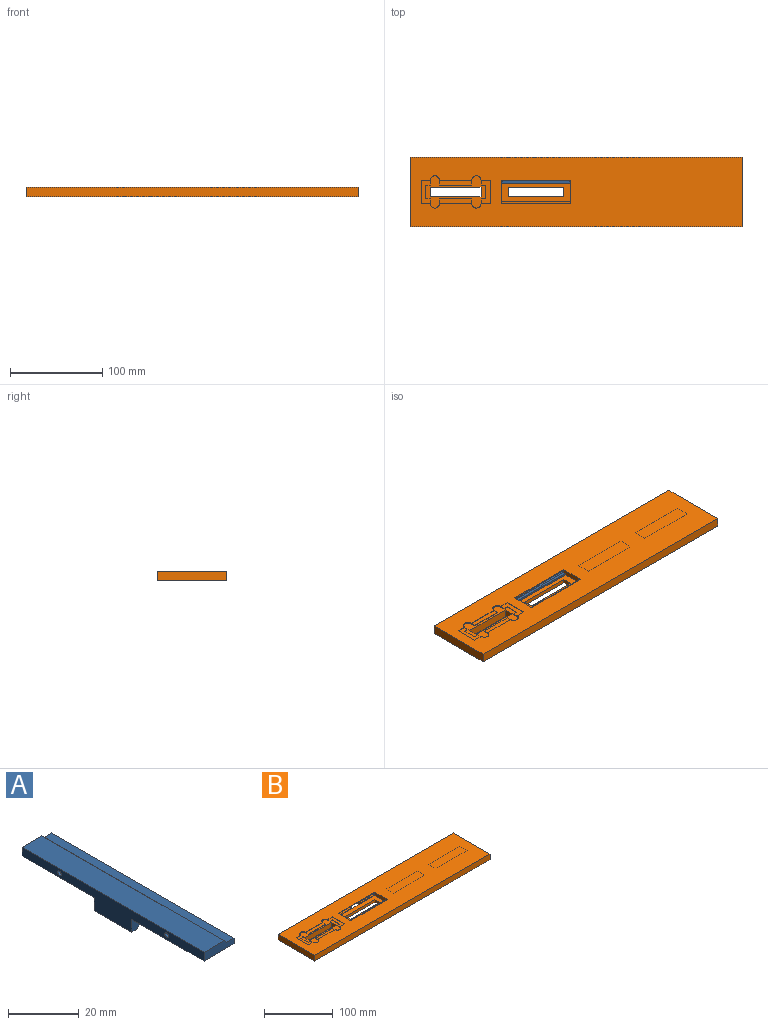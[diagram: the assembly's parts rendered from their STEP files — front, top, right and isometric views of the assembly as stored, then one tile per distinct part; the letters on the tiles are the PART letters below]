
ASSEMBLY  parts=2 mates=1
PART A: 16 faces, bbox 12x73x7.5 mm
  f0: plane 73x7.5mm, normal (-1,0,0), area 283mm2, adj f1,f2,f3,f4,f8,f9,f10,f12
  f1: plane 73x8mm, normal (0,0,1), area 584mm2, adj f0,f3,f4,f5
  f2: plane 73x12mm, normal (0,0,-1), area 801mm2, adj f0,f3,f4,f7,f8,f9,f11
  f3: plane 12x3mm, normal (0,-1,0), area 32.5mm2, adj f0,f1,f2,f5,f6,f7
  f4: plane 12x3mm, normal (0,1,0), area 32.5mm2, adj f0,f1,f2,f5,f6,f7
  f5: plane 73x1mm, normal (0.71,0,0.71), area 103.2mm2, adj f1,f3,f4,f6
  f6: plane 73x3mm, normal (0,0,1), area 219mm2, adj f3,f4,f5,f7
  f7: plane 73x2mm, normal (1,0,0), area 146mm2, adj f2,f3,f4,f6
  f8: plane 5x4.5mm, normal (0,1,0), area 16.6mm2, adj f0,f2,f10,f11
  f9: plane 5x4.5mm, normal (0,-1,0), area 16.6mm2, adj f0,f2,f10,f11
  f10: plane 15x2mm, normal (0,0,-1), area 30mm2, adj f0,f8,f9,f11
  f11: cylinder r=15mm len=15mm, axis (0,1,0), area 81.6mm2, adj f2,f8,f9,f10
  f12: cylinder r=0.75mm len=1.5mm, axis (-1,0,0), area 4.7mm2, adj f0,f13
  f13: plane 1.5x1.5mm, normal (-1,0,0), area 1.8mm2, adj f12
  f14: cylinder r=0.75mm len=1.5mm, axis (-1,0,0), area 4.7mm2, adj f0,f15
  f15: plane 1.5x1.5mm, normal (-1,0,0), area 1.8mm2, adj f14
PART B: 75 faces, bbox 360x75x10 mm
  f0: plane 26.5x15mm, normal (0,0,1), area 397.5mm2, adj f4,f50,f53,f57
  f1: plane 26x5.5mm, normal (1,0,0), area 133.2mm2, adj f3,f4,f11,f19,f54,f55
  f2: plane 26x5.5mm, normal (-1,0,0), area 133.2mm2, adj f3,f4,f11,f19,f54,f55
  f3: plane 75x23mm, normal (0,0,1), area 1125mm2, adj f1,f2,f4,f55,f56,f59,f60,f61
  f4: plane 75x5.5mm, normal (0,-1,0), area 168.5mm2, adj f0,f1,f2,f3,f11,f49,f50,f51
  f5: plane 65x35mm, normal (0,0,1), area 782.1mm2, adj f25,f26,f27,f28,f29,f30,f31,f32
  f6: plane 360x75mm, normal (0,0,-1), area 25550mm2, adj f15,f16,f17,f18,f45,f46,f47,f48
  f7: plane 10x0.5mm, normal (0,-1,0), area 5mm2, adj f11,f14,f21,f43
  f8: plane 35x0.5mm, normal (0,-1,0), area 17.5mm2, adj f11,f24,f43,f44
  f9: plane 35x0.5mm, normal (0,1,0), area 17.5mm2, adj f11,f12,f41,f42
  f10: plane 10x0.5mm, normal (0,1,0), area 5mm2, adj f11,f14,f21,f42
  f11: plane 360x75mm, normal (0,0,1), area 23017.9mm2, adj f1,f2,f4,f7,f8,f9,f10,f15
  f12: plane 35x5mm, normal (0,0,1), area 175mm2, adj f9,f30,f31,f32
  f13: plane 25x10mm, normal (0,0,1), area 175mm2, adj f20,f22,f23,f33,f34,f35,f36,f37
  f14: plane 25x10mm, normal (0,0,1), area 175mm2, adj f7,f10,f21,f25,f26,f27,f28,f29
  f15: plane 360x10mm, normal (0,1,0), area 3600mm2, adj f6,f11,f16,f18
  f16: plane 75x10mm, normal (-1,0,0), area 750mm2, adj f6,f11,f15,f17
  f17: plane 360x10mm, normal (0,-1,0), area 3600mm2, adj f6,f11,f16,f18
  f18: plane 75x10mm, normal (1,0,0), area 750mm2, adj f6,f11,f15,f17
  f19: plane 75x2.25mm, normal (0,1,0), area 168.8mm2, adj f1,f2,f11,f54
  f20: plane 10x0.5mm, normal (0,-1,0), area 5mm2, adj f11,f13,f23,f44
  f21: plane 25x0.5mm, normal (1,0,0), area 12.5mm2, adj f7,f10,f11,f14
  f22: plane 10x0.5mm, normal (0,1,0), area 5mm2, adj f11,f13,f23,f41
  f23: plane 25x0.5mm, normal (-1,0,0), area 12.5mm2, adj f11,f13,f20,f22
  f24: plane 35x5mm, normal (0,0,1), area 175mm2, adj f8,f38,f39,f40
  f25: plane 5x0.5mm, normal (1,0,0), area 2.5mm2, adj f5,f14,f26,f43
  f26: plane 5x0.5mm, normal (0,-1,0), area 2.5mm2, adj f5,f14,f25,f27
  f27: plane 15x0.5mm, normal (1,0,0), area 7.5mm2, adj f5,f14,f26,f28
  f28: plane 5x0.5mm, normal (0,1,0), area 2.5mm2, adj f5,f14,f27,f29
  f29: plane 5x0.5mm, normal (1,0,0), area 2.5mm2, adj f5,f14,f28,f42
  f30: plane 5x0.5mm, normal (-1,0,0), area 2.5mm2, adj f5,f12,f31,f42
  f31: plane 35x0.5mm, normal (0,1,0), area 17.5mm2, adj f5,f12,f30,f32
  f32: plane 5x0.5mm, normal (1,0,0), area 2.5mm2, adj f5,f12,f31,f41
  f33: plane 5x0.5mm, normal (-1,0,0), area 2.5mm2, adj f5,f13,f34,f41
  f34: plane 5x0.5mm, normal (0,1,0), area 2.5mm2, adj f5,f13,f33,f35
  f35: plane 15x0.5mm, normal (-1,0,0), area 7.5mm2, adj f5,f13,f34,f36
  f36: plane 5x0.5mm, normal (0,-1,0), area 2.5mm2, adj f5,f13,f35,f37
  f37: plane 5x0.5mm, normal (-1,0,0), area 2.5mm2, adj f5,f13,f36,f44
  f38: plane 5x0.5mm, normal (1,0,0), area 2.5mm2, adj f5,f24,f39,f44
  f39: plane 35x0.5mm, normal (0,-1,0), area 17.5mm2, adj f5,f24,f38,f40
  f40: plane 5x0.5mm, normal (-1,0,0), area 2.5mm2, adj f5,f24,f39,f43
  f41: cylinder r=5mm len=10mm, axis (0,0,-1), area 15.7mm2, adj f5,f9,f11,f22,f32,f33
  f42: cylinder r=5mm len=10mm, axis (0,0,-1), area 15.7mm2, adj f5,f9,f10,f11,f29,f30
  f43: cylinder r=5mm len=10mm, axis (0,0,1), area 15.7mm2, adj f5,f7,f8,f11,f25,f40
  f44: cylinder r=5mm len=10mm, axis (0,0,1), area 15.7mm2, adj f5,f8,f11,f20,f37,f38
  f45: plane 55x9mm, normal (0,-1,0), area 495mm2, adj f5,f6,f46,f48
  f46: plane 10x9mm, normal (1,0,0), area 90mm2, adj f5,f6,f45,f47
  f47: plane 55x9mm, normal (0,1,0), area 495mm2, adj f5,f6,f46,f48
  f48: plane 10x9mm, normal (-1,0,0), area 90mm2, adj f5,f6,f45,f47
  f49: plane 73x15mm, normal (0,0,-1), area 1095mm2, adj f4,f50,f52,f53
  f50: plane 15x3mm, normal (1,0,0), area 45mm2, adj f0,f4,f49,f53
  f51: plane 26.5x15mm, normal (0,0,1), area 397.5mm2, adj f4,f52,f53,f58
  f52: plane 15x3mm, normal (-1,0,0), area 45mm2, adj f4,f49,f51,f53
  f53: plane 73x8.75mm, normal (0,-1,0), area 334mm2, adj f0,f6,f49,f50,f51,f52,f57,f58
  f54: plane 75x3mm, normal (0,0,1), area 225mm2, adj f1,f2,f19,f55
  f55: plane 75x3.25mm, normal (0,1,0), area 243.7mm2, adj f1,f2,f3,f54
  f56: plane 20x4.5mm, normal (0,1,0), area 90mm2, adj f3,f6,f57,f58
  f57: plane 15x5.75mm, normal (1,0,0), area 86.3mm2, adj f0,f4,f6,f53,f56
  f58: plane 15x5.75mm, normal (-1,0,0), area 86.3mm2, adj f4,f6,f51,f53,f56
  f59: plane 10x4.5mm, normal (1,0,0), area 45mm2, adj f3,f6,f60,f61
  f60: plane 60x4.5mm, normal (0,-1,0), area 270mm2, adj f3,f6,f59,f62
  f61: plane 60x4.5mm, normal (0,1,0), area 270mm2, adj f3,f6,f59,f62
  f62: plane 10x4.5mm, normal (-1,0,0), area 45mm2, adj f3,f6,f60,f61
  f63: plane 15x0.5mm, normal (-1,0,0), area 7.5mm2, adj f64,f66,f67,f68
  f64: plane 65x0.5mm, normal (0,-1,0), area 32.5mm2, adj f63,f65,f67,f68
  f65: plane 15x0.5mm, normal (1,0,0), area 7.5mm2, adj f64,f66,f67,f68
  f66: plane 65x0.5mm, normal (0,1,0), area 32.5mm2, adj f63,f65,f67,f68
  f67: plane 65x15mm, normal (0,0,1), area 975mm2, adj f63,f64,f65,f66
  f68: plane 65x15mm, normal (0,0,-1), area 975mm2, adj f63,f64,f65,f66
  f69: plane 15x0.5mm, normal (-1,0,0), area 7.5mm2, adj f70,f72,f73,f74
  f70: plane 65x0.5mm, normal (0,-1,0), area 32.5mm2, adj f69,f71,f73,f74
  f71: plane 15x0.5mm, normal (1,0,0), area 7.5mm2, adj f70,f72,f73,f74
  f72: plane 65x0.5mm, normal (0,1,0), area 32.5mm2, adj f69,f71,f73,f74
  f73: plane 65x15mm, normal (0,0,1), area 975mm2, adj f69,f70,f71,f72
  f74: plane 65x15mm, normal (0,0,-1), area 975mm2, adj f69,f70,f71,f72
PLACE A rot(axis=(0,0,-1),90deg) t=(-21.13,-18.06,25.45)mm
PLACE B t=(22.37,-34.56,23.7)mm
MATE parallel A.f4 <-> B.f52  axis (1,0,0) through (15.37,-22.06,25.95)mm
